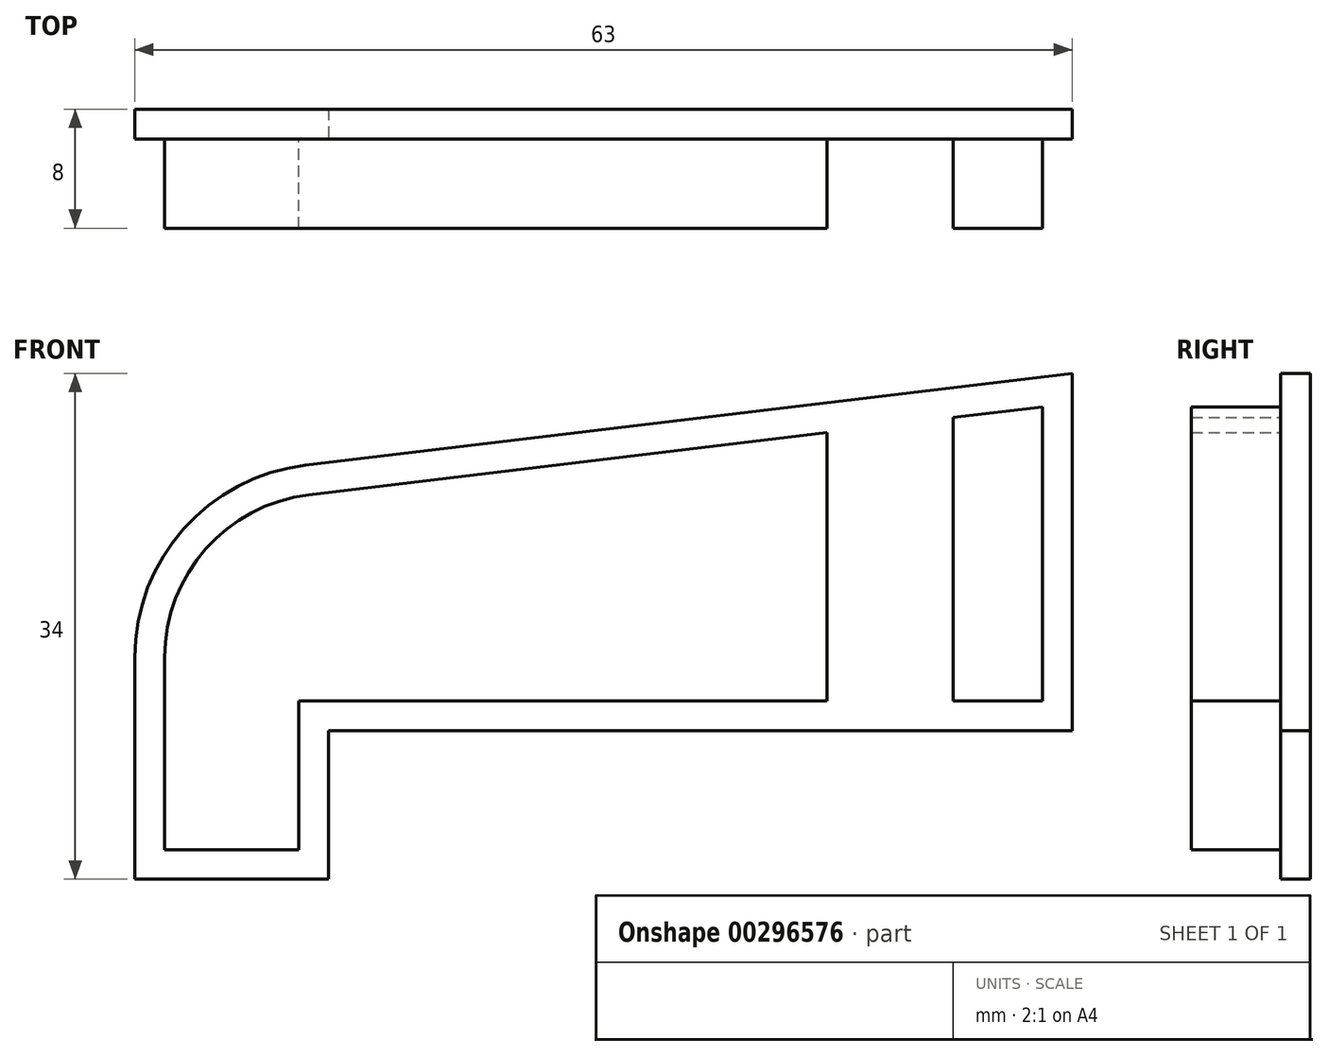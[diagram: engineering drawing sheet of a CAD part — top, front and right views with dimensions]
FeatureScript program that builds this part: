
annotation { "Feature Type Name" : "Feature", "Feature Type Description" : "" }
export const myFeature = defineFeature(function(context is Context, id is Id, definition is map)
    precondition{}
    {
        {
            var Q0;
            Q0=qCreatedBy(makeId("Front.planeOp"),FACE);
            var sketch = newSketch(context, id + "F0", { "sketchPlane" : qUnion([Q0])});
            skLineSegment(sketch, "E0", {"start": v(0, 0) * mm, "end": v(40, 0) * mm});
            skLineSegment(sketch, "E1", {"start": v(40, 0) * mm, "end": v(40, 24) * mm});
            skLineSegment(sketch, "E2", {"start": v(40, 24) * mm, "end": v(-11.55, 17.81) * mm});
            skArc(sketch, "E3", {"start": v(-11.55, 17.81) * mm, "mid": v(-19.72, 13.53) * mm, "end": v(-23, 4.9) * mm});
            skLineSegment(sketch, "E4", {"start": v(-23, 4.9) * mm, "end": v(-23, -10) * mm});
            skLineSegment(sketch, "E5", {"start": v(-23, -10) * mm, "end": v(-10, -10) * mm});
            skLineSegment(sketch, "E6", {"start": v(-10, -10) * mm, "end": v(-10, 0) * mm});
            skLineSegment(sketch, "E7", {"start": v(-10, 0) * mm, "end": v(0, 0) * mm});
            skLineSegment(sketch, "E8", {"start": v(-10, 0) * mm, "end": v(-10, 18) * mm});
            skSolve(sketch);
        }
        {
            var Q0;
            {var subQ0=sQuery(id+"F0.wireOp",EDGE,"E3");Q0=makeQuery(id+"F0.imprint","IMPRINT",FACE,{"disambiguationData":[TD([[makeQuery(id+"F0.imprint","IMPRINT",EDGE,{"derivedFrom":subQ0}),1.0]])]});}
            var Q1;
            Q1=makeQuery(id+"F0.imprint","IMPRINT",FACE,{"disambiguationData":[TD([[makeQuery(id+"F0.imprint","IMPRINT",EDGE,{"derivedFrom":sQuery(id+"F0.wireOp",EDGE,"E0")}),1.0]])]});
            extrude(context, id + "F1", {"entities" : qUnion([Q0, Q1]), "oppositeDirection" : true, "depth" : (2) * mm});
        }
        {
            var Q0;
            Q0=makeQuery(id+"F0.imprint","IMPRINT",FACE,{"disambiguationData":[TD([[makeQuery(id+"F0.imprint","IMPRINT",EDGE,{"derivedFrom":sQuery(id+"F0.wireOp",EDGE,"E0")}),1.0]])]});
            var sketch = newSketch(context, id + "F2", { "sketchPlane" : qUnion([Q0])});
            skLineSegment(sketch, "E9.0", {"start": v(38, 2) * mm, "end": v(38, 21.75) * mm});
            skLineSegment(sketch, "E9.1", {"start": v(0, 2) * mm, "end": v(38, 2) * mm});
            skLineSegment(sketch, "E9.2", {"start": v(38, 21.75) * mm, "end": v(-11.31, 15.83) * mm});
            skLineSegment(sketch, "E9.3", {"start": v(-12, 2) * mm, "end": v(0, 2) * mm});
            skArc(sketch, "E9.4", {"start": v(-11.31, 15.83) * mm, "mid": v(-18.23, 12.2) * mm, "end": v(-21, 4.9) * mm});
            skLineSegment(sketch, "E9.5", {"start": v(-21, 4.9) * mm, "end": v(-21, -8) * mm});
            skLineSegment(sketch, "E9.6", {"start": v(-21, -8) * mm, "end": v(-12, -8) * mm});
            skLineSegment(sketch, "E9.7", {"start": v(-12, -8) * mm, "end": v(-12, 2) * mm});
            skSolve(sketch);
        }
        {
            var Q0;
            Q0 = qSketchRegion(id + "F2", true);
            extrude(context, id + "F3", {"entities" : qUnion([Q0]), "operationType" : NewBodyOperationType.ADD, "depth" : 6 * mm});
        }
        {
            var Q0;
            Q0=makeQuery(id+"F3.opExtrude","CAP_FACE",FACE,{"disambiguationData":[OSD([sQuery(id+"F2.wireOp",EDGE,"E9.0"),sQuery(id+"F2.wireOp",EDGE,"E9.1"),sQuery(id+"F2.wireOp",EDGE,"E9.2"),sQuery(id+"F2.wireOp",EDGE,"E9.3"),sQuery(id+"F2.wireOp",EDGE,"E9.4"),sQuery(id+"F2.wireOp",EDGE,"E9.5"),sQuery(id+"F2.wireOp",EDGE,"E9.6"),sQuery(id+"F2.wireOp",EDGE,"E9.7")])],"isStart":false});
            var sketch = newSketch(context, id + "F4", { "sketchPlane" : qUnion([Q0])});
            skLineSegment(sketch, "E10.0", {"start": v(38, 2) * mm, "end": v(38, 21.75) * mm});
            skLineSegment(sketch, "E11", {"start": v(32, 22.9) * mm, "end": v(32, -3.1) * mm});
            skLineSegment(sketch, "E12", {"start": v(23.5, 22.9) * mm, "end": v(23.5, -3.1) * mm});
            skLineSegment(sketch, "E13", {"start": v(23.5, 22.9) * mm, "end": v(32, 22.9) * mm});
            skLineSegment(sketch, "E14", {"start": v(23.5, -3.1) * mm, "end": v(32, -3.1) * mm});
            skSolve(sketch);
        }
        {
            var Q0;
            Q0 = qSketchRegion(id + "F4", true);
            extrude(context, id + "F5", {"entities" : qUnion([Q0]), "operationType" : NewBodyOperationType.REMOVE, "oppositeDirection" : true, "depth" : 6 * mm});
        }
    });
